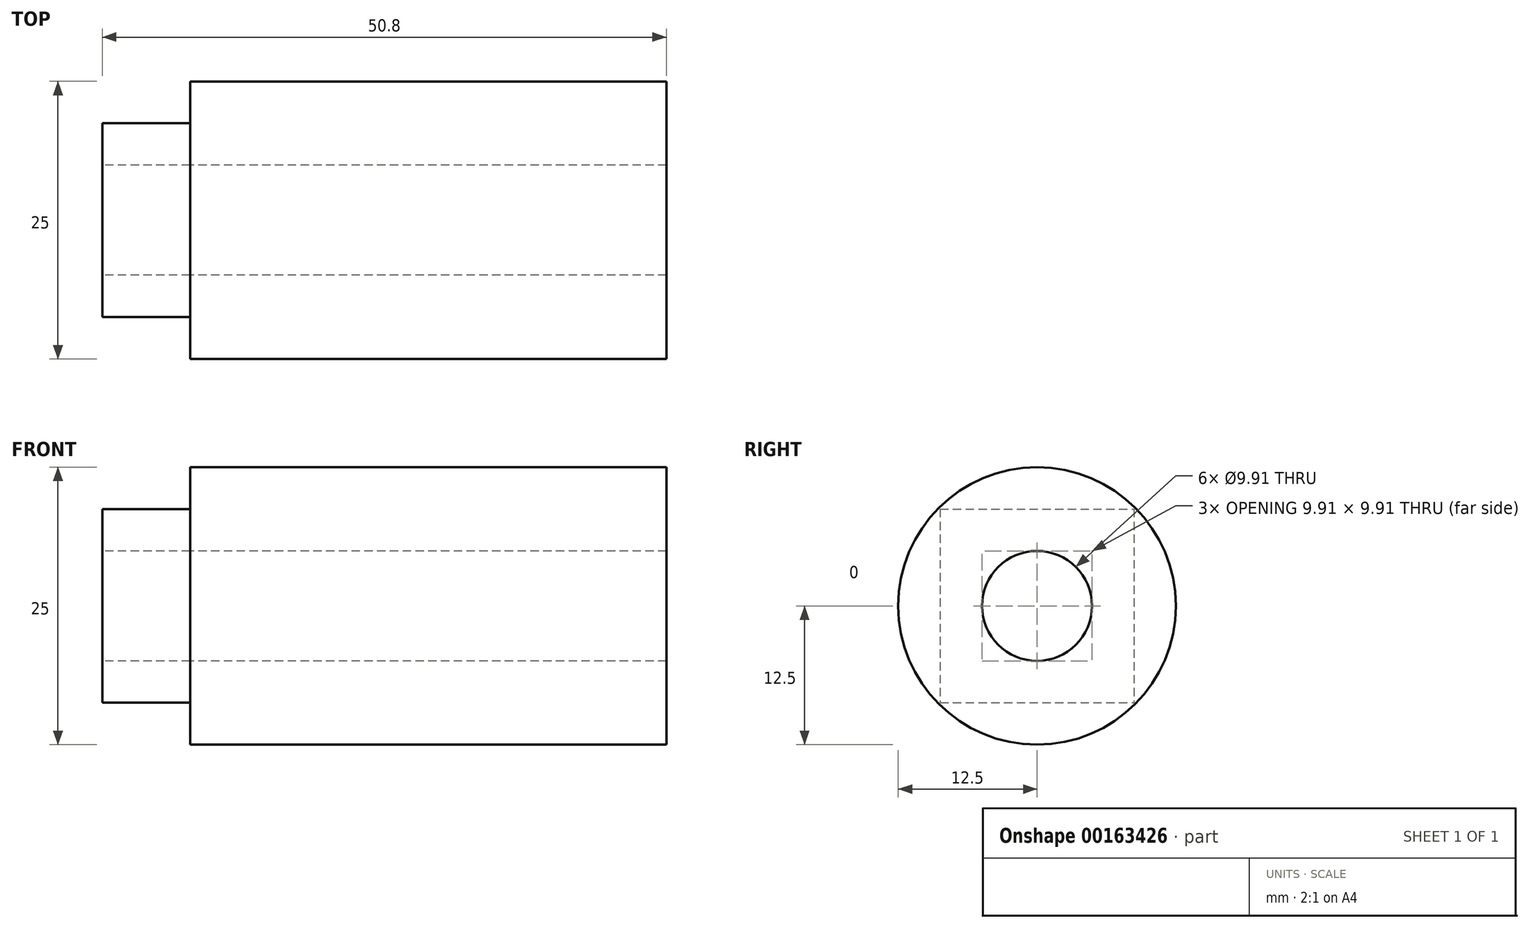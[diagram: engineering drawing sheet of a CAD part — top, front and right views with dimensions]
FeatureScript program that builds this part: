
annotation { "Feature Type Name" : "Feature", "Feature Type Description" : "" }
export const myFeature = defineFeature(function(context is Context, id is Id, definition is map)
    precondition{}
    {
        {
            var Q0;
            Q0=qCreatedBy(makeId("Right.planeOp"),FACE);
            var sketch = newSketch(context, id + "F0", { "sketchPlane" : qUnion([Q0])});
            skLineSegment(sketch, "E0.bottom", {"start": v(-8.72, 8.72) * mm, "end": v(8.72, 8.72) * mm});
            skLineSegment(sketch, "E0.top", {"start": v(-8.72, -8.72) * mm, "end": v(8.72, -8.72) * mm});
            skLineSegment(sketch, "E0.left", {"start": v(-8.72, 8.72) * mm, "end": v(-8.72, -8.72) * mm});
            skLineSegment(sketch, "E0.right", {"start": v(8.72, 8.72) * mm, "end": v(8.72, -8.72) * mm});
            skPoint(sketch, "E0.middle", {"position": v(0, 0) * mm});
            skCircle(sketch, "E1", {"center": v(0, 0) * mm, "radius": 12.5 * mm});
            skSolve(sketch);
        }
        {
            var Q0;
            Q0=makeQuery(id+"F0.imprint","IMPRINT",FACE,{"disambiguationData":[TD([[makeQuery(id+"F0.imprint","IMPRINT",EDGE,{"derivedFrom":sQuery(id+"F0.wireOp",EDGE,"E0.bottom")}),-1.0]])]});
            extrude(context, id + "F1", {"entities" : qUnion([Q0]), "oppositeDirection" : true, "depth" : 7.9 * mm});
        }
        {
            var Q0;
            Q0=makeQuery(id+"F0.imprint","IMPRINT",FACE,{"disambiguationData":[TD([[makeQuery(id+"F0.imprint","IMPRINT",EDGE,{"derivedFrom":sQuery(id+"F0.wireOp",EDGE,"E0.bottom")}),1.0]])]});
            var Q1;
            Q1=makeQuery(id+"F0.imprint","IMPRINT",FACE,{"disambiguationData":[TD([[makeQuery(id+"F0.imprint","IMPRINT",EDGE,{"derivedFrom":sQuery(id+"F0.wireOp",EDGE,"E0.bottom")}),-1.0]])]});
            extrude(context, id + "F2", {"entities" : qUnion([Q0, Q1]), "depth" : 42.9 * mm});
        }
        {
            var Q0;
            Q0=makeQuery(id+"F1.opExtrude","CAP_FACE",FACE,{"disambiguationData":[OSD([sQuery(id+"F0.wireOp",EDGE,"E0.bottom"),sQuery(id+"F0.wireOp",EDGE,"E0.top"),sQuery(id+"F0.wireOp",EDGE,"E0.left"),sQuery(id+"F0.wireOp",EDGE,"E0.right")])],"isStart":false});
            var sketch = newSketch(context, id + "F3", { "sketchPlane" : qUnion([Q0])});
            skCircle(sketch, "E2", {"center": v(0, 0) * mm, "radius": 4.95 * mm});
            skSolve(sketch);
        }
        {
            var Q0;
            Q0=makeQuery(id+"F3.imprint","IMPRINT",FACE,{"disambiguationData":[TD([[makeQuery(id+"F3.imprint","IMPRINT",EDGE,{"derivedFrom":sQuery(id+"F3.wireOp",EDGE,"E2")}),1.0]])]});
            extrude(context, id + "F4", {"entities" : qUnion([Q0]), "operationType" : NewBodyOperationType.REMOVE, "oppositeDirection" : true, "depth" : 50.8 * mm});
        }
    });
